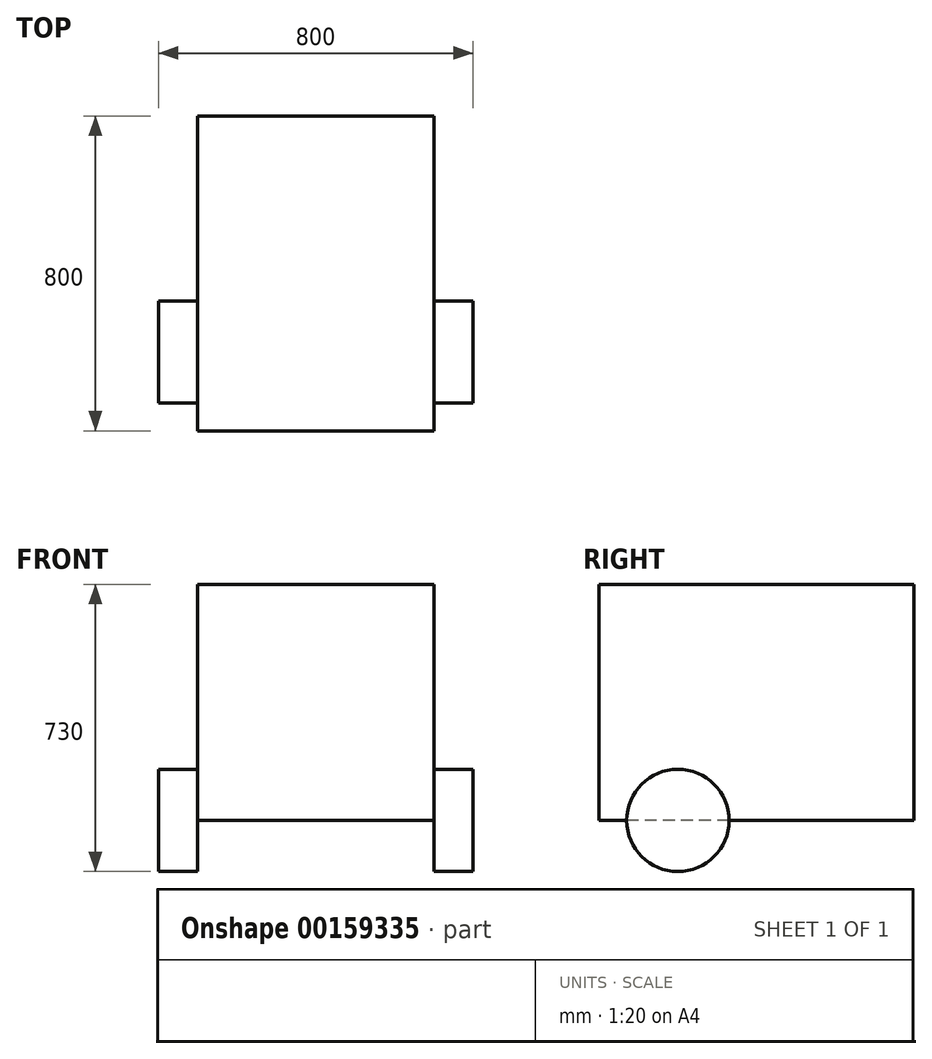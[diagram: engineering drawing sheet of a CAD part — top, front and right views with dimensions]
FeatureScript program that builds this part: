
annotation { "Feature Type Name" : "Feature", "Feature Type Description" : "" }
export const myFeature = defineFeature(function(context is Context, id is Id, definition is map)
    precondition{}
    {
        {
            assignVariable(context, id + "F0", {"name" : "GenBodyW", "anyValue" : 560});
        }
        {
            assignVariable(context, id + "F1", {"name" : "GenWheelW", "anyValue" : 100});
        }
        {
            var Q0;
            Q0=qCreatedBy(makeId("Right.planeOp"),FACE);
            var sketch = newSketch(context, id + "F2", { "sketchPlane" : qUnion([Q0])});
            skLineSegment(sketch, "E0.bottom", {"start": v(400, -300) * mm, "end": v(-400, -300) * mm});
            skLineSegment(sketch, "E0.top", {"start": v(400, 300) * mm, "end": v(-400, 300) * mm});
            skLineSegment(sketch, "E0.left", {"start": v(400, -300) * mm, "end": v(400, 300) * mm});
            skLineSegment(sketch, "E0.right", {"start": v(-400, -300) * mm, "end": v(-400, 300) * mm});
            skPoint(sketch, "E0.middle", {"position": v(0, 0) * mm});
            skCircle(sketch, "E1", {"center": v(-200, -300) * mm, "radius": 130 * mm});
            skSolve(sketch);
        }
        {
            var Q0;
            Q0=makeQuery(id+"F2.imprint","IMPRINT",FACE,{"disambiguationData":[TD([[makeQuery(id+"F2.imprint","IMPRINT",EDGE,{"derivedFrom":sQuery(id+"F2.wireOp",EDGE,"E0.top")}),1.0]])]});
            var Q1;
            {var subQ0=sQuery(id+"F2.wireOp",EDGE,"E1");var subQ1=sQuery(id+"F2.wireOp",EDGE,"E0.bottom");var subQ2=makeQuery(id+"F2.imprint","INTERSECT",VERTEX,{"disambiguationData":[OD(0.0)],"derivedFrom":[subQ1,subQ0]});Q1=makeQuery(id+"F2.imprint","IMPRINT",FACE,{"disambiguationData":[TD([[makeQuery(id+"F2.imprint","IMPRINT",EDGE,{"disambiguationData":[TD([[subQ2,-1.0]])],"derivedFrom":subQ1}),-1.0]])]});}
            extrude(context, id + "F3", {"entities" : qUnion([Q0, Q1]), "depth" : (getVariable(context, 'GenBodyW')) * mm});
        }
        {
            var Q0;
            {var subQ0=sQuery(id+"F2.wireOp",EDGE,"E1");var subQ1=sQuery(id+"F2.wireOp",EDGE,"E0.bottom");var subQ2=makeQuery(id+"F2.imprint","INTERSECT",VERTEX,{"disambiguationData":[OD(0.0)],"derivedFrom":[subQ1,subQ0]});Q0=makeQuery(id+"F2.imprint","IMPRINT",FACE,{"disambiguationData":[TD([[makeQuery(id+"F2.imprint","IMPRINT",EDGE,{"disambiguationData":[TD([[subQ2,-1.0]])],"derivedFrom":subQ1}),1.0]])]});}
            var Q1;
            {var subQ0=sQuery(id+"F2.wireOp",EDGE,"E1");var subQ1=sQuery(id+"F2.wireOp",EDGE,"E0.bottom");var subQ2=makeQuery(id+"F2.imprint","INTERSECT",VERTEX,{"disambiguationData":[OD(0.0)],"derivedFrom":[subQ1,subQ0]});Q1=makeQuery(id+"F2.imprint","IMPRINT",FACE,{"disambiguationData":[TD([[makeQuery(id+"F2.imprint","IMPRINT",EDGE,{"disambiguationData":[TD([[subQ2,-1.0]])],"derivedFrom":subQ1}),-1.0]])]});}
            extrude(context, id + "F4", {"entities" : qUnion([Q0, Q1]), "operationType" : NewBodyOperationType.ADD, "oppositeDirection" : true, "depth" : (getVariable(context, 'GenWheelW')) * mm});
        }
        {
            var Q0;
            Q0=makeQuery(id+"F3.opExtrude","CAP_FACE",FACE,{"disambiguationData":[OSD([sQuery(id+"F2.wireOp",EDGE,"E0.bottom"),sQuery(id+"F2.wireOp",EDGE,"E0.top"),sQuery(id+"F2.wireOp",EDGE,"E0.left"),sQuery(id+"F2.wireOp",EDGE,"E0.right")])],"isStart":true});
            cPlane(context, id + "F5", {"entities" : qUnion([Q0]), "cplaneType" : CPlaneType.OFFSET, "offset" : 300 * mm, "oppositeDirection" : true, "width" : 150 * mm, "height" : 150 * mm});
        }
        {
            var Q0;
            Q0=makeQuery(id+"F3.opExtrude","SWEPT_BODY",BODY,{"disambiguationData":[OSD([sQuery(id+"F2.wireOp",EDGE,"E0.bottom"),sQuery(id+"F2.wireOp",EDGE,"E0.top"),sQuery(id+"F2.wireOp",EDGE,"E0.left"),sQuery(id+"F2.wireOp",EDGE,"E0.right")])]});
            var Q1;
            Q1=qCreatedBy(id+"F5.planeOp",FACE);
            mirror(context, id + "F6", {"operationType" : NewBodyOperationType.ADD, "entities" : qUnion([Q0]), "mirrorPlane" : qUnion([Q1])});
        }
    });
